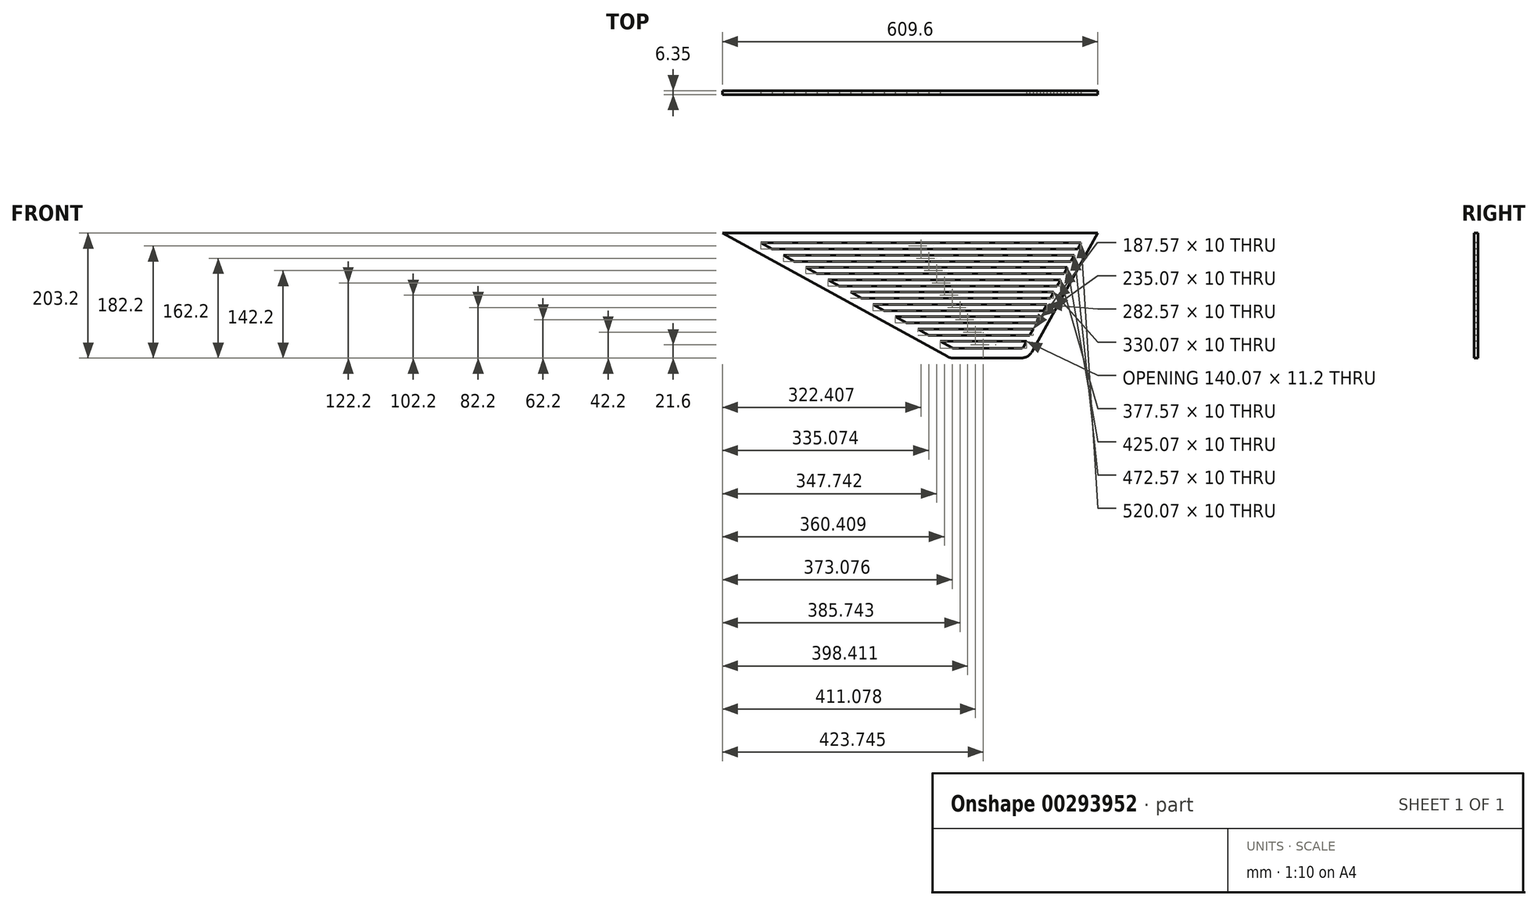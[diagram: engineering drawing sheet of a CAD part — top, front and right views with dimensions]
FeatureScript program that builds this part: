
annotation { "Feature Type Name" : "Feature", "Feature Type Description" : "" }
export const myFeature = defineFeature(function(context is Context, id is Id, definition is map)
    precondition{}
    {
        {
            var Q0;
            Q0=qCreatedBy(makeId("Front.planeOp"),FACE);
            var sketch = newSketch(context, id + "F0", { "sketchPlane" : qUnion([Q0])});
            skLineSegment(sketch, "E0", {"start": v(-304.8, 0) * mm, "end": v(304.8, 0) * mm});
            skLineSegment(sketch, "E1", {"start": v(-304.8, 0) * mm, "end": v(60.7, -200.73) * mm});
            skLineSegment(sketch, "E2", {"start": v(70.33, -203.2) * mm, "end": v(180.42, -203.2) * mm});
            skLineSegment(sketch, "E3", {"start": v(197.91, -192.9) * mm, "end": v(304.8, 0) * mm});
            skPoint(sketch, "E4.visualSharp", {"position": v(65.2, -203.2) * mm});
            skArc(sketch, "E4.filletArc", {"start": v(60.7, -200.73) * mm, "mid": v(65.36, -202.57) * mm, "end": v(70.33, -203.2) * mm});
            skPoint(sketch, "E5.visualSharp", {"position": v(192.2, -203.2) * mm});
            skArc(sketch, "E5.filletArc", {"start": v(180.42, -203.2) * mm, "mid": v(190.57, -200.43) * mm, "end": v(197.91, -192.9) * mm});
            skSolve(sketch);
        }
        {
            var Q0;
            Q0 = qSketchRegion(id + "F0", true);
            extrude(context, id + "F1", {"entities" : qUnion([Q0]), "depth" : 6.35 * mm, "offsetDistance" : 25 * mm, "symmetric" : true});
        }
        {
            var Q0;
            Q0=makeQuery(id+"F1.opExtrude","CAP_FACE",FACE,{"disambiguationData":[OSD([sQuery(id+"F0.wireOp",EDGE,"E0"),sQuery(id+"F0.wireOp",EDGE,"E1"),sQuery(id+"F0.wireOp",EDGE,"E2"),sQuery(id+"F0.wireOp",EDGE,"E3"),sQuery(id+"F0.wireOp",EDGE,"E4.filletArc"),sQuery(id+"F0.wireOp",EDGE,"E5.filletArc")])],"isStart":false});
            var sketch = newSketch(context, id + "F2", { "sketchPlane" : qUnion([Q0])});
            skLineSegment(sketch, "E6.0", {"start": v(-242.43, -16) * mm, "end": v(277.64, -16) * mm});
            skArc(sketch, "E6.1", {"start": v(68.4, -186.7) * mm, "mid": v(69.34, -187.07) * mm, "end": v(70.33, -187.2) * mm});
            skLineSegment(sketch, "E6.2", {"start": v(70.33, -187.2) * mm, "end": v(180.42, -187.2) * mm});
            skLineSegment(sketch, "E6.3", {"start": v(-242.43, -16) * mm, "end": v(-224.22, -26) * mm});
            skArc(sketch, "E6.4", {"start": v(180.42, -187.2) * mm, "mid": v(182.45, -186.65) * mm, "end": v(183.92, -185.14) * mm});
            skLineSegment(sketch, "E6.5", {"start": v(183.92, -185.14) * mm, "end": v(188.98, -176) * mm});
            skLineSegment(sketch, "E7", {"start": v(-206.01, -36) * mm, "end": v(266.56, -36) * mm});
            skLineSegment(sketch, "E8", {"start": v(-224.22, -26) * mm, "end": v(272.1, -26) * mm});
            skLineSegment(sketch, "E9.trimOffspring", {"start": v(-206.01, -36) * mm, "end": v(-187.8, -46) * mm});
            skLineSegment(sketch, "E10.trimOffspring", {"start": v(272.1, -26) * mm, "end": v(277.64, -16) * mm});
            skLineSegment(sketch, "E11", {"start": v(-187.8, -46) * mm, "end": v(261.02, -46) * mm});
            skLineSegment(sketch, "E12", {"start": v(-169.6, -56) * mm, "end": v(255.48, -56) * mm});
            skLineSegment(sketch, "E13.trimOffspring", {"start": v(-169.6, -56) * mm, "end": v(-151.38, -66) * mm});
            skLineSegment(sketch, "E14.trimOffspring", {"start": v(261.02, -46) * mm, "end": v(266.56, -36) * mm});
            skLineSegment(sketch, "E15", {"start": v(-151.38, -66) * mm, "end": v(249.93, -66) * mm});
            skLineSegment(sketch, "E16.0.1.0", {"start": v(-133.18, -76) * mm, "end": v(244.4, -76) * mm});
            skLineSegment(sketch, "E16.0.2.0", {"start": v(-114.97, -86) * mm, "end": v(238.85, -86) * mm});
            skLineSegment(sketch, "E16.0.3.0", {"start": v(-96.76, -96) * mm, "end": v(233.31, -96) * mm});
            skLineSegment(sketch, "E16.0.4.0", {"start": v(-78.55, -106) * mm, "end": v(227.77, -106) * mm});
            skLineSegment(sketch, "E16.0.5.0", {"start": v(-60.34, -116) * mm, "end": v(222.23, -116) * mm});
            skLineSegment(sketch, "E16.0.6.0", {"start": v(-42.13, -126) * mm, "end": v(216.69, -126) * mm});
            skLineSegment(sketch, "E16.0.7.0", {"start": v(-23.92, -136) * mm, "end": v(211.15, -136) * mm});
            skLineSegment(sketch, "E16.0.8.0", {"start": v(-5.72, -146) * mm, "end": v(205.6, -146) * mm});
            skLineSegment(sketch, "E16.0.9.0", {"start": v(12.5, -156) * mm, "end": v(200.06, -156) * mm});
            skLineSegment(sketch, "E16.0.10.0", {"start": v(30.7, -166) * mm, "end": v(194.52, -166) * mm});
            skLineSegment(sketch, "E16.0.11.0", {"start": v(48.91, -176) * mm, "end": v(188.98, -176) * mm});
            skLineSegment(sketch, "E16.direction1", {"start": v(-151.38, -66) * mm, "end": v(-126.38, -66) * mm, "construction": true});
            skLineSegment(sketch, "E16.direction2", {"start": v(-151.38, -66) * mm, "end": v(-151.38, -76) * mm, "construction": true});
            skPoint(sketch, "E17.orphan", {"position": v(-151.38, -186) * mm});
            skPoint(sketch, "E18.orphan", {"position": v(-151.38, -176) * mm});
            skPoint(sketch, "E19.orphan", {"position": v(-151.38, -166) * mm});
            skPoint(sketch, "E20.orphan", {"position": v(-151.38, -156) * mm});
            skPoint(sketch, "E21.orphan", {"position": v(-151.38, -146) * mm});
            skPoint(sketch, "E22.orphan", {"position": v(-151.38, -136) * mm});
            skPoint(sketch, "E23.orphan", {"position": v(-151.38, -126) * mm});
            skPoint(sketch, "E24.orphan", {"position": v(-151.38, -116) * mm});
            skPoint(sketch, "E25.orphan", {"position": v(-151.38, -106) * mm});
            skPoint(sketch, "E26.orphan", {"position": v(-151.38, -96) * mm});
            skPoint(sketch, "E27.orphan", {"position": v(-151.38, -86) * mm});
            skPoint(sketch, "E28.orphan", {"position": v(249.93, -186) * mm});
            skPoint(sketch, "E29.orphan", {"position": v(249.93, -176) * mm});
            skPoint(sketch, "E30.orphan", {"position": v(249.93, -156) * mm});
            skPoint(sketch, "E31.orphan", {"position": v(249.93, -166) * mm});
            skPoint(sketch, "E32.orphan", {"position": v(249.93, -146) * mm});
            skPoint(sketch, "E33.orphan", {"position": v(249.93, -136) * mm});
            skPoint(sketch, "E34.orphan", {"position": v(249.93, -126) * mm});
            skPoint(sketch, "E35.orphan", {"position": v(249.93, -116) * mm});
            skPoint(sketch, "E36.orphan", {"position": v(249.93, -106) * mm});
            skPoint(sketch, "E37.orphan", {"position": v(249.93, -96) * mm});
            skPoint(sketch, "E38.orphan", {"position": v(249.93, -86) * mm});
            skPoint(sketch, "E39.orphan", {"position": v(249.93, -76) * mm});
            skLineSegment(sketch, "E40.trimOffspring", {"start": v(194.52, -166) * mm, "end": v(200.06, -156) * mm});
            skLineSegment(sketch, "E41.trimOffspring", {"start": v(48.91, -176) * mm, "end": v(68.4, -186.7) * mm});
            skLineSegment(sketch, "E42.trimOffspring", {"start": v(12.5, -156) * mm, "end": v(30.7, -166) * mm});
            skLineSegment(sketch, "E43.trimOffspring", {"start": v(205.6, -146) * mm, "end": v(211.15, -136) * mm});
            skLineSegment(sketch, "E44.trimOffspring", {"start": v(216.69, -126) * mm, "end": v(222.23, -116) * mm});
            skLineSegment(sketch, "E45.trimOffspring", {"start": v(-23.92, -136) * mm, "end": v(-5.72, -146) * mm});
            skLineSegment(sketch, "E46.trimOffspring", {"start": v(227.77, -106) * mm, "end": v(233.31, -96) * mm});
            skLineSegment(sketch, "E47.trimOffspring", {"start": v(238.85, -86) * mm, "end": v(244.4, -76) * mm});
            skLineSegment(sketch, "E48.trimOffspring", {"start": v(249.93, -66) * mm, "end": v(255.48, -56) * mm});
            skLineSegment(sketch, "E49.trimOffspring", {"start": v(-60.34, -116) * mm, "end": v(-42.13, -126) * mm});
            skLineSegment(sketch, "E50.trimOffspring", {"start": v(-96.76, -96) * mm, "end": v(-78.55, -106) * mm});
            skLineSegment(sketch, "E51.trimOffspring", {"start": v(-133.18, -76) * mm, "end": v(-114.97, -86) * mm});
            skSolve(sketch);
        }
        {
            var Q0;
            Q0 = qSketchRegion(id + "F2", true);
            extrude(context, id + "F3", {"entities" : qUnion([Q0]), "operationType" : NewBodyOperationType.REMOVE, "endBound" : BoundingType.THROUGH_ALL, "oppositeDirection" : true, "depth" : 25 * mm, "offsetDistance" : 25 * mm});
        }
    });
